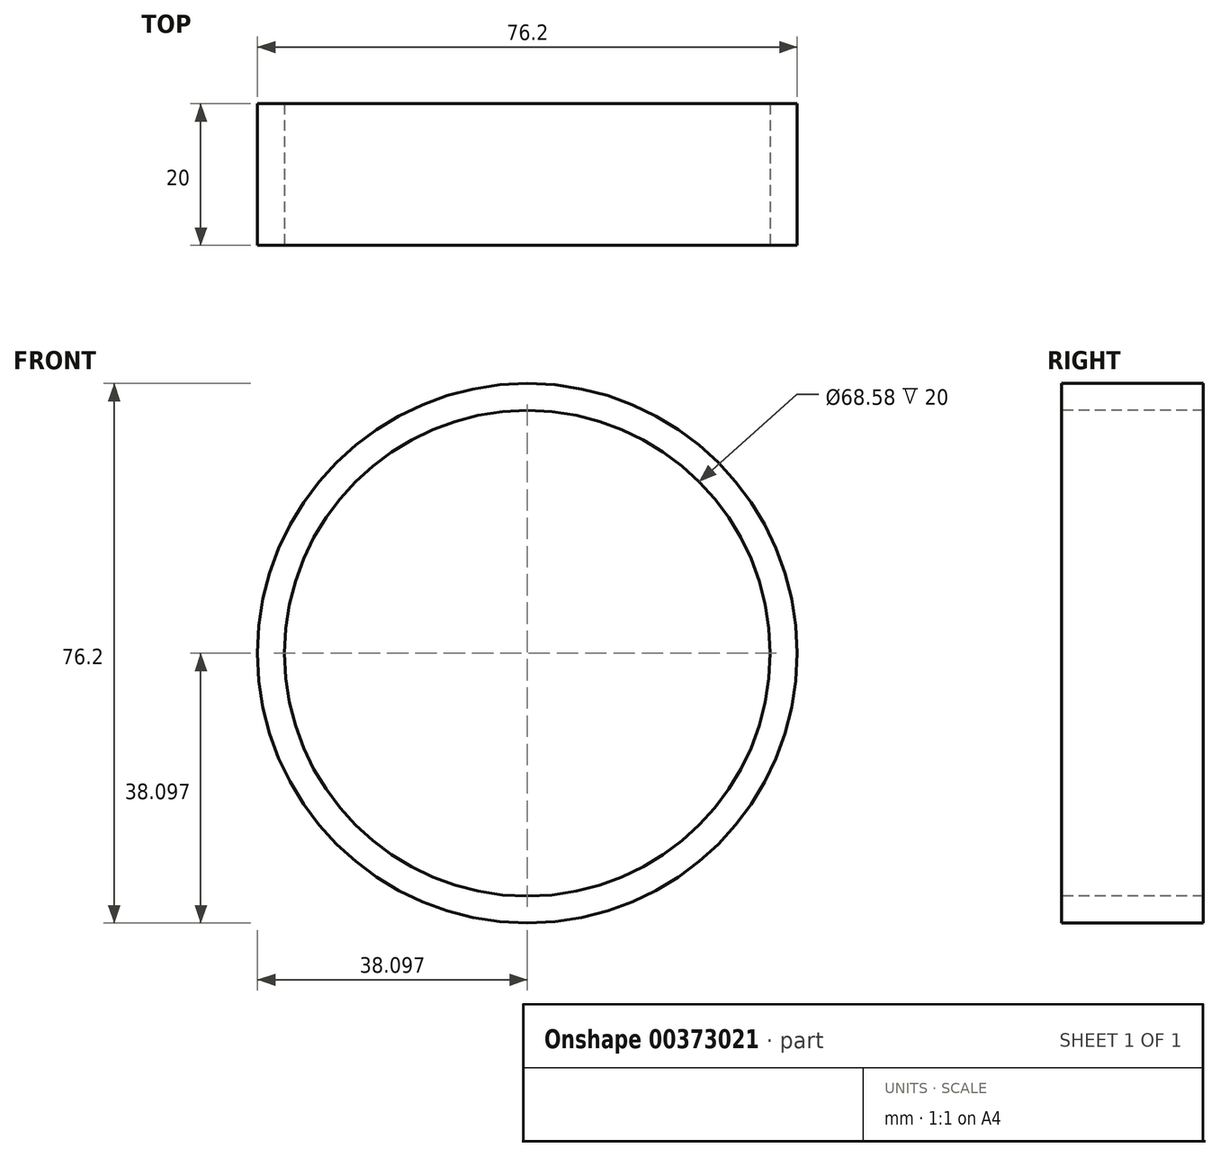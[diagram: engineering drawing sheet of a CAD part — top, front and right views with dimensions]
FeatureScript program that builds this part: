
annotation { "Feature Type Name" : "Feature", "Feature Type Description" : "" }
export const myFeature = defineFeature(function(context is Context, id is Id, definition is map)
    precondition{}
    {
        {
            var Q0;
            Q0=qCreatedBy(makeId("Front.planeOp"),FACE);
            var sketch = newSketch(context, id + "F0", { "sketchPlane" : qUnion([Q0])});
            skCircle(sketch, "E0", {"center": v(-26.73, 27.15) * mm, "radius": 38.1 * mm});
            skLineSegment(sketch, "E1", {"start": v(-26.73, 27.15) * mm, "end": v(-26.73, 65.25) * mm});
            skSolve(sketch);
        }
        {
            var Q0;
            Q0=makeQuery(id+"F0.imprint","IMPRINT",FACE,{"disambiguationData":[TD([[makeQuery(id+"F0.imprint","IMPRINT",EDGE,{"derivedFrom":sQuery(id+"F0.wireOp",EDGE,"E0")}),1.0]])]});
            extrude(context, id + "F1", {"entities" : qUnion([Q0]), "depth" : 20 * mm});
        }
        {
            var Q0;
            Q0=makeQuery(id+"F1.opExtrude","CAP_FACE",FACE,{"disambiguationData":[OSD([sQuery(id+"F0.wireOp",EDGE,"E0")])],"isStart":false});
            var sketch = newSketch(context, id + "F2", { "sketchPlane" : qUnion([Q0])});
            skCircle(sketch, "E2", {"center": v(-26.73, 27.15) * mm, "radius": 121.78 * mm});
            skSolve(sketch);
        }
        {
            var Q0;
            Q0=sQuery(id+"F2.wireOp",VERTEX,"E2.center");
            var Q1;
            Q1=makeQuery(id+"F1.opExtrude","SWEPT_BODY",BODY,{"disambiguationData":[OSD([sQuery(id+"F0.wireOp",EDGE,"E0")])]});
            hole(context, id + "F3", {"style" : HoleStyle.SIMPLE, "endStyle" : HoleEndStyle.THROUGH, "holeDiameter" : 68.58 * mm, "locations" : qUnion([Q0]), "scope" : qUnion([Q1]), "tappedDepth" : 12.7 * mm, "tapClearance" : 3});
        }
    });
